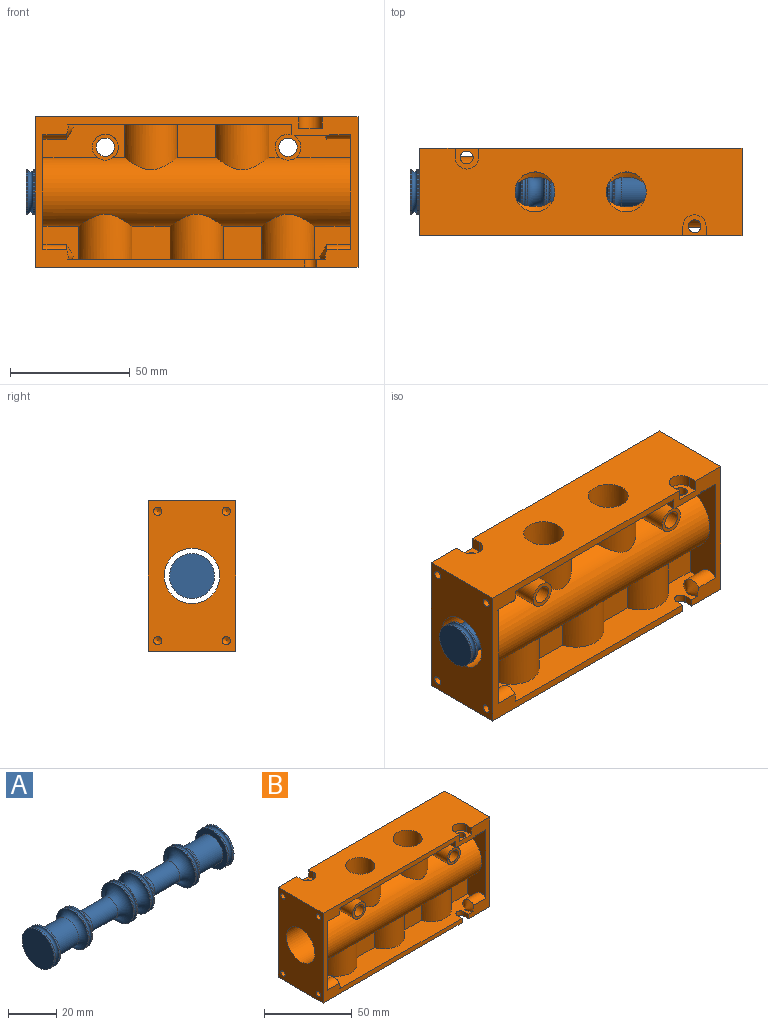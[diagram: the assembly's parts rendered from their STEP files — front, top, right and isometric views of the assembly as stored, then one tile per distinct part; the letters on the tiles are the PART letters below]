
ASSEMBLY  parts=2 mates=1
PART A: 33 faces, bbox 105.2x27.4x27.4 mm
  f0: torus R=9.4mm, axis (1,0,0), area 512.8mm2, adj f1,f17
  f1: cylinder r=9.4mm len=18.8mm, axis (1,0,0), area 30mm2, adj f0,f2
  f2: torus R=9.4mm, axis (1,0,0), area 134.1mm2, adj f1,f3
  f3: cylinder r=9.4mm len=18.8mm, axis (1,0,0), area 30mm2, adj f2,f4
  f4: torus R=9.4mm, axis (1,0,0), area 292.7mm2, adj f3,f5
  f5: cylinder r=4.83mm len=14.73mm, axis (1,0,0), area 446.7mm2, adj f4,f6
  f6: torus R=9.4mm, axis (1,0,0), area 292.7mm2, adj f5,f7
  f7: cylinder r=9.4mm len=18.8mm, axis (1,0,0), area 30mm2, adj f6,f8
  f8: torus R=9.4mm, axis (1,0,0), area 134.1mm2, adj f7,f9
  f9: cylinder r=9.4mm len=18.8mm, axis (1,0,0), area 30mm2, adj f8,f10
  f10: torus R=9.4mm, axis (1,0,0), area 211.2mm2, adj f9,f11
  f11: cylinder r=6.58mm len=13.44mm, axis (1,0,0), area 556.2mm2, adj f10,f12
  f12: plane 18.8x18.8mm, normal (1,0,0), area 141.2mm2, adj f11,f13
  f13: cylinder r=9.4mm len=18.8mm, axis (1,0,0), area 45mm2, adj f12,f14
  f14: torus R=9.4mm, axis (1,0,0), area 185.6mm2, adj f13,f15
  f15: cylinder r=9.4mm len=18.8mm, axis (1,0,0), area 45mm2, adj f14,f16
  f16: plane 18.8x18.8mm, normal (-1,0,0), area 277.5mm2, adj f15
  f17: cylinder r=9.4mm len=18.8mm, axis (-1,0,0), area 30mm2, adj f0,f18
  f18: torus R=9.4mm, axis (-1,0,0), area 134.1mm2, adj f17,f19
  f19: cylinder r=9.4mm len=18.8mm, axis (-1,0,0), area 30mm2, adj f18,f20
  f20: torus R=9.4mm, axis (-1,0,0), area 292.7mm2, adj f19,f21
  f21: cylinder r=4.83mm len=14.73mm, axis (-1,0,0), area 446.7mm2, adj f20,f22
  f22: torus R=9.4mm, axis (-1,0,0), area 292.7mm2, adj f21,f23
  f23: cylinder r=9.4mm len=18.8mm, axis (-1,0,0), area 30mm2, adj f22,f24
  f24: torus R=9.4mm, axis (-1,0,0), area 134.1mm2, adj f23,f25
  f25: cylinder r=9.4mm len=18.8mm, axis (-1,0,0), area 30mm2, adj f24,f26
  f26: torus R=9.4mm, axis (-1,0,0), area 211.2mm2, adj f25,f27
  f27: cylinder r=6.58mm len=13.44mm, axis (-1,0,0), area 556.2mm2, adj f26,f28
  f28: plane 18.8x18.8mm, normal (-1,0,0), area 141.2mm2, adj f27,f29
  f29: cylinder r=9.4mm len=18.8mm, axis (-1,0,0), area 45mm2, adj f28,f30
  f30: torus R=9.4mm, axis (-1,0,0), area 185.6mm2, adj f29,f31
  f31: cylinder r=9.4mm len=18.8mm, axis (-1,0,0), area 45mm2, adj f30,f32
  f32: plane 18.8x18.8mm, normal (1,0,0), area 277.5mm2, adj f31
PART B: 132 faces, bbox 135.9x39.6x65 mm
  f0: cylinder r=14.73mm len=128.27mm, axis (-1,0,0), area 4299.8mm2, adj f1,f112,f113,f114,f115,f116,f117,f118
  f1: plane 56.39x14.99mm, normal (1,0,0), area 504.6mm2, adj f0,f2,f105,f106,f110,f111,f112,f130
  f2: plane 128.27x14.99mm, normal (0,0,-1), area 1314.7mm2, adj f1,f3,f4,f5,f6,f104,f105,f106
  f3: cylinder r=4.9mm len=9.89mm, axis (1,0,0), area 132.4mm2, adj f2,f4,f106,f122
  f4: cone r=1.64mm half-angle=59deg, axis (1,0,0), area 55.6mm2, adj f2,f3,f106
  f5: plane 4.31x3.81mm, normal (1,0,0), area 16.4mm2, adj f2,f6,f106,f131
  f6: cylinder r=8mm len=15.23mm, axis (0,0,1), area 96.6mm2, adj f2,f5,f7,f104,f105,f131
  f7: plane 14.86x11.81mm, normal (0,0,-1), area 120.5mm2, adj f6,f8,f9,f10,f105,f106,f131
  f8: plane 0.55x0.5mm, normal (-1,0,0), area 0.1mm2, adj f7,f105,f106
  f9: cone r=1.64mm half-angle=59deg, axis (-1,0,0), area 7.3mm2, adj f7,f105
  f10: cylinder r=2.67mm len=5.33mm, axis (0,0,1), area 53.2mm2, adj f7,f11
  f11: plane 9.65x8.64mm, normal (0,0,1), area 51mm2, adj f10,f12,f102,f103,f106
  f12: plane 4.76x3.81mm, normal (1,0,0), area 18.1mm2, adj f11,f13,f103,f106
  f13: plane 134.62x36.32mm, normal (0,0,1), area 4306.6mm2, adj f12,f14,f85,f86,f87,f88,f91,f100
  f14: plane 62.74x36.32mm, normal (1,0,0), area 1821.7mm2, adj f13,f15,f72,f77,f79,f81,f83,f88
  f15: plane 134.62x36.32mm, normal (0,0,-1), area 4172.1mm2, adj f14,f16,f19,f22,f25,f26,f27,f69
  f16: cylinder r=8.33mm len=20.32mm, axis (0,0,-1), area 1062.2mm2, adj f15,f17,f18,f72
  f17: cone r=0mm half-angle=59deg, axis (0,0,-1), area 28.5mm2, adj f16,f72
  f18: cone r=0mm half-angle=59deg, axis (0,0,-1), area 28.5mm2, adj f16,f72
  f19: cylinder r=8.33mm len=20.32mm, axis (0,0,-1), area 1062.2mm2, adj f15,f20,f21,f72
  f20: cone r=0mm half-angle=59deg, axis (0,0,-1), area 28.5mm2, adj f19,f72
  f21: cone r=0mm half-angle=59deg, axis (0,0,-1), area 28.5mm2, adj f19,f72
  f22: cylinder r=8.33mm len=20.32mm, axis (0,0,-1), area 1062.2mm2, adj f15,f23,f24,f72
  f23: cone r=0mm half-angle=59deg, axis (0,0,-1), area 28.5mm2, adj f22,f72
  f24: cone r=0mm half-angle=59deg, axis (0,0,-1), area 28.5mm2, adj f22,f72
  f25: cylinder r=2.67mm len=5.33mm, axis (0,0,1), area 26.6mm2, adj f15,f26,f71,f111
  f26: plane 3.81x3.18mm, normal (1,0,0), area 12.1mm2, adj f15,f25,f106,f111
  f27: plane 3.81x3.18mm, normal (1,0,0), area 12.1mm2, adj f15,f28,f69,f88
  f28: plane 128.27x14.99mm, normal (0,0,1), area 1288.4mm2, adj f27,f29,f30,f31,f32,f33,f61,f62
  f29: cylinder r=4.9mm len=9.89mm, axis (1,0,0), area 132.4mm2, adj f28,f30,f68,f88
  f30: cone r=1.64mm half-angle=59deg, axis (1,0,0), area 55.6mm2, adj f28,f29,f88
  f31: cone r=1.64mm half-angle=59deg, axis (-1,0,0), area 55.6mm2, adj f28,f32,f88
  f32: cylinder r=4.9mm len=9.89mm, axis (-1,0,0), area 132.4mm2, adj f28,f31,f33,f88
  f33: plane 56.39x14.99mm, normal (1,0,0), area 504.6mm2, adj f28,f32,f34,f36,f53,f57,f61,f88
  f34: cylinder r=4.9mm len=9.89mm, axis (-1,0,0), area 132.4mm2, adj f33,f35,f36,f88
  f35: cone r=1.64mm half-angle=59deg, axis (-1,0,0), area 55.6mm2, adj f34,f36,f88
  f36: plane 128.27x14.99mm, normal (0,0,-1), area 1314.7mm2, adj f33,f34,f35,f37,f39,f40,f42,f49
  f37: cylinder r=11.51mm len=22.12mm, axis (0,0,1), area 491.9mm2, adj f36,f38,f39,f52,f57
  f38: cone r=1.64mm half-angle=59deg, axis (0,0,1), area 0mm2, adj f37,f57
  f39: plane 15.98x13.81mm, normal (0,-1,0), area 220.6mm2, adj f36,f37,f40,f57
  f40: cylinder r=11.51mm len=22.12mm, axis (0,0,1), area 491.9mm2, adj f36,f39,f41,f53,f57
  f41: cone r=1.64mm half-angle=59deg, axis (0,0,1), area 0mm2, adj f40,f57
  f42: plane 4.31x3.81mm, normal (-1,0,0), area 16.4mm2, adj f36,f43,f49,f88
  f43: cylinder r=5.4mm len=14.99mm, axis (0,1,0), area 484.8mm2, adj f42,f44,f49,f52,f57,f88
  f44: plane 14.86x11.81mm, normal (0,0,-1), area 120.5mm2, adj f43,f45,f46,f47,f49,f51,f88
  f45: plane 0.55x0.5mm, normal (1,0,0), area 0.1mm2, adj f44,f51,f88
  f46: cone r=1.64mm half-angle=59deg, axis (1,0,0), area 7.3mm2, adj f44,f51
  f47: cylinder r=2.67mm len=5.33mm, axis (0,0,1), area 53.2mm2, adj f44,f48
  f48: plane 9.65x8.64mm, normal (0,0,1), area 51mm2, adj f47,f85,f86,f87,f88
  f49: cylinder r=8mm len=15.23mm, axis (0,0,1), area 96.6mm2, adj f36,f42,f43,f44,f50,f51
  f50: cone r=1.64mm half-angle=59deg, axis (1,0,0), area 1.1mm2, adj f36,f49,f51
  f51: cylinder r=4.9mm len=9.89mm, axis (1,0,0), area 131.1mm2, adj f36,f44,f45,f46,f49,f50,f68,f88
  f52: plane 34.02x13.81mm, normal (0,-1,0), area 383.3mm2, adj f36,f37,f43,f57,f68
  f53: plane 34.02x13.81mm, normal (0,-1,0), area 383.3mm2, adj f33,f36,f40,f54,f57
  f54: cylinder r=5.4mm len=14.99mm, axis (0,1,0), area 492.1mm2, adj f53,f55,f57
  f55: plane 10.8x10.8mm, normal (0,-1,0), area 45.9mm2, adj f54,f56
  f56: cylinder r=3.81mm len=36.32mm, axis (0,-1,0), area 869.5mm2, adj f55,f106
  f57: cylinder r=14.73mm len=128.27mm, axis (-1,0,0), area 4299.8mm2, adj f33,f37,f38,f39,f40,f41,f43,f52
  f58: cone r=1.64mm half-angle=59deg, axis (0,0,-1), area 0mm2, adj f57,f66
  f59: cone r=1.64mm half-angle=59deg, axis (0,0,-1), area 0mm2, adj f57,f64
  f60: cone r=1.64mm half-angle=59deg, axis (0,0,-1), area 0mm2, adj f57,f62
  f61: plane 14.97x13.81mm, normal (0,-1,0), area 206.7mm2, adj f28,f33,f57,f62
  f62: cylinder r=11.51mm len=22.12mm, axis (0,0,-1), area 491.9mm2, adj f28,f57,f60,f61,f63
  f63: plane 15.98x13.81mm, normal (0,-1,0), area 220.6mm2, adj f28,f57,f62,f64
  f64: cylinder r=11.51mm len=22.12mm, axis (0,0,-1), area 491.9mm2, adj f28,f57,f59,f63,f65
  f65: plane 15.98x13.81mm, normal (0,-1,0), area 220.6mm2, adj f28,f57,f64,f66
  f66: cylinder r=11.51mm len=22.12mm, axis (0,0,-1), area 491.9mm2, adj f28,f57,f58,f65,f67
  f67: plane 14.97x13.81mm, normal (0,-1,0), area 206.7mm2, adj f28,f57,f66,f68
  f68: plane 56.39x14.99mm, normal (-1,0,0), area 504.6mm2, adj f28,f29,f36,f51,f52,f57,f67,f88
  f69: cylinder r=2.67mm len=5.33mm, axis (0,0,1), area 26.6mm2, adj f15,f27,f28,f70
  f70: plane 3.81x3.18mm, normal (-1,0,0), area 12.1mm2, adj f15,f28,f69,f88
  f71: plane 3.81x3.18mm, normal (-1,0,0), area 12.1mm2, adj f15,f25,f106,f111
  f72: cylinder r=11.56mm len=134.62mm, axis (-1,0,0), area 8899.5mm2, adj f14,f16,f17,f18,f19,f20,f21,f22
  f73: cone r=0mm half-angle=59deg, axis (0,0,1), area 28.5mm2, adj f72,f101
  f74: cone r=0mm half-angle=59deg, axis (0,0,1), area 28.5mm2, adj f72,f101
  f75: cone r=0mm half-angle=59deg, axis (0,0,1), area 28.5mm2, adj f72,f100
  f76: cone r=0mm half-angle=59deg, axis (0,0,1), area 28.5mm2, adj f72,f100
  f77: cylinder r=1.73mm len=11.27mm, axis (1,0,0), area 122.3mm2, adj f14,f78
  f78: cone r=0mm half-angle=59deg, axis (1,0,0), area 10.9mm2, adj f77
  f79: cylinder r=1.73mm len=11.27mm, axis (1,0,0), area 122.3mm2, adj f14,f80
  f80: cone r=0mm half-angle=59deg, axis (1,0,0), area 10.9mm2, adj f79
  f81: cylinder r=1.73mm len=11.27mm, axis (1,0,0), area 122.3mm2, adj f14,f82
  f82: cone r=0mm half-angle=59deg, axis (1,0,0), area 10.9mm2, adj f81
  f83: cylinder r=1.73mm len=11.27mm, axis (1,0,0), area 122.3mm2, adj f14,f84
  f84: cone r=0mm half-angle=59deg, axis (1,0,0), area 10.9mm2, adj f83
  f85: plane 4.76x3.81mm, normal (-1,0,0), area 18.1mm2, adj f13,f48,f86,f88
  f86: cylinder r=4.83mm len=9.65mm, axis (0,0,1), area 72.2mm2, adj f13,f48,f85,f87
  f87: plane 4.76x3.81mm, normal (1,0,0), area 18.1mm2, adj f13,f48,f86,f88
  f88: plane 135.88x63.99mm, normal (0,-1,0), area 1438.9mm2, adj f13,f14,f15,f27,f28,f29,f30,f31
  f89: cylinder r=3.81mm len=36.32mm, axis (0,-1,0), area 869.5mm2, adj f88,f90
  f90: plane 10.8x10.8mm, normal (0,1,0), area 45.9mm2, adj f89,f123
  f91: plane 62.74x36.32mm, normal (-1,0,0), area 1821.7mm2, adj f13,f15,f72,f88,f92,f94,f96,f98
  f92: cylinder r=1.73mm len=11.27mm, axis (-1,0,0), area 122.3mm2, adj f91,f93
  f93: cone r=0mm half-angle=59deg, axis (-1,0,0), area 10.9mm2, adj f92
  f94: cylinder r=1.73mm len=11.27mm, axis (-1,0,0), area 122.3mm2, adj f91,f95
  f95: cone r=0mm half-angle=59deg, axis (-1,0,0), area 10.9mm2, adj f94
  f96: cylinder r=1.73mm len=11.27mm, axis (-1,0,0), area 122.3mm2, adj f91,f97
  f97: cone r=0mm half-angle=59deg, axis (-1,0,0), area 10.9mm2, adj f96
  f98: cylinder r=1.73mm len=11.27mm, axis (-1,0,0), area 122.3mm2, adj f91,f99
  f99: cone r=0mm half-angle=59deg, axis (-1,0,0), area 10.9mm2, adj f98
  f100: cylinder r=8.33mm len=20.32mm, axis (0,0,1), area 1060.5mm2, adj f13,f72,f75,f76
  f101: cylinder r=8.33mm len=20.32mm, axis (0,0,1), area 1060.5mm2, adj f13,f72,f73,f74
  f102: plane 4.76x3.81mm, normal (-1,0,0), area 18.1mm2, adj f11,f13,f103,f106
  f103: cylinder r=4.83mm len=9.65mm, axis (0,0,1), area 72.2mm2, adj f11,f12,f13,f102
  f104: cone r=1.64mm half-angle=59deg, axis (-1,0,0), area 1.1mm2, adj f2,f6,f105
  f105: cylinder r=4.9mm len=9.89mm, axis (-1,0,0), area 131.1mm2, adj f1,f2,f6,f7,f8,f9,f104,f106
  f106: plane 135.88x63.99mm, normal (0,1,0), area 1438.9mm2, adj f1,f2,f3,f4,f5,f7,f8,f11
  f107: cylinder r=4.9mm len=9.89mm, axis (1,0,0), area 132.4mm2, adj f106,f108,f111,f122
  f108: cone r=1.64mm half-angle=59deg, axis (1,0,0), area 55.6mm2, adj f106,f107,f111
  f109: cone r=1.64mm half-angle=59deg, axis (-1,0,0), area 55.6mm2, adj f106,f110,f111
  f110: cylinder r=4.9mm len=9.89mm, axis (-1,0,0), area 132.4mm2, adj f1,f106,f109,f111
  f111: plane 128.27x14.99mm, normal (0,0,1), area 1288.5mm2, adj f1,f25,f26,f71,f106,f107,f108,f109
  f112: plane 14.97x13.81mm, normal (0,1,0), area 206.7mm2, adj f0,f1,f111,f114
  f113: cone r=1.64mm half-angle=59deg, axis (0,0,-1), area 0mm2, adj f0,f114
  f114: cylinder r=11.51mm len=22.12mm, axis (0,0,-1), area 491.9mm2, adj f0,f111,f112,f113,f115
  f115: plane 15.98x13.81mm, normal (0,1,0), area 220.6mm2, adj f0,f111,f114,f117
  f116: cone r=1.64mm half-angle=59deg, axis (0,0,-1), area 0mm2, adj f0,f117
  f117: cylinder r=11.51mm len=22.12mm, axis (0,0,-1), area 491.9mm2, adj f0,f111,f115,f116,f118
  f118: plane 15.98x13.81mm, normal (0,1,0), area 220.6mm2, adj f0,f111,f117,f120
  f119: cone r=1.64mm half-angle=59deg, axis (0,0,-1), area 0mm2, adj f0,f120
  f120: cylinder r=11.51mm len=22.12mm, axis (0,0,-1), area 491.9mm2, adj f0,f111,f118,f119,f121
  f121: plane 14.97x13.81mm, normal (0,1,0), area 206.7mm2, adj f0,f111,f120,f122
  f122: plane 56.39x14.99mm, normal (-1,0,0), area 504.6mm2, adj f0,f2,f3,f106,f107,f111,f121,f124
  f123: cylinder r=5.4mm len=14.99mm, axis (0,1,0), area 492.1mm2, adj f0,f90,f124
  f124: plane 34.02x13.81mm, normal (0,1,0), area 383.3mm2, adj f0,f2,f122,f123,f126
  f125: cone r=1.64mm half-angle=59deg, axis (0,0,1), area 0mm2, adj f0,f126
  f126: cylinder r=11.51mm len=22.12mm, axis (0,0,1), area 491.9mm2, adj f0,f2,f124,f125,f127
  f127: plane 15.98x13.81mm, normal (0,1,0), area 220.6mm2, adj f0,f2,f126,f129
  f128: cone r=1.64mm half-angle=59deg, axis (0,0,1), area 0mm2, adj f0,f129
  f129: cylinder r=11.51mm len=22.12mm, axis (0,0,1), area 491.9mm2, adj f0,f2,f127,f128,f130
  f130: plane 34.02x13.81mm, normal (0,1,0), area 383.3mm2, adj f0,f1,f2,f129,f131
  f131: cylinder r=5.4mm len=14.99mm, axis (0,1,0), area 484.9mm2, adj f0,f5,f6,f7,f106,f130
PLACE A t=(-18.61,0,-31.37)mm
PLACE B t=(0,0,-31.37)mm
MATE slider B.f0 <-> A.f0  axis (1,0,0) through (67.31,0,-31.37)mm
